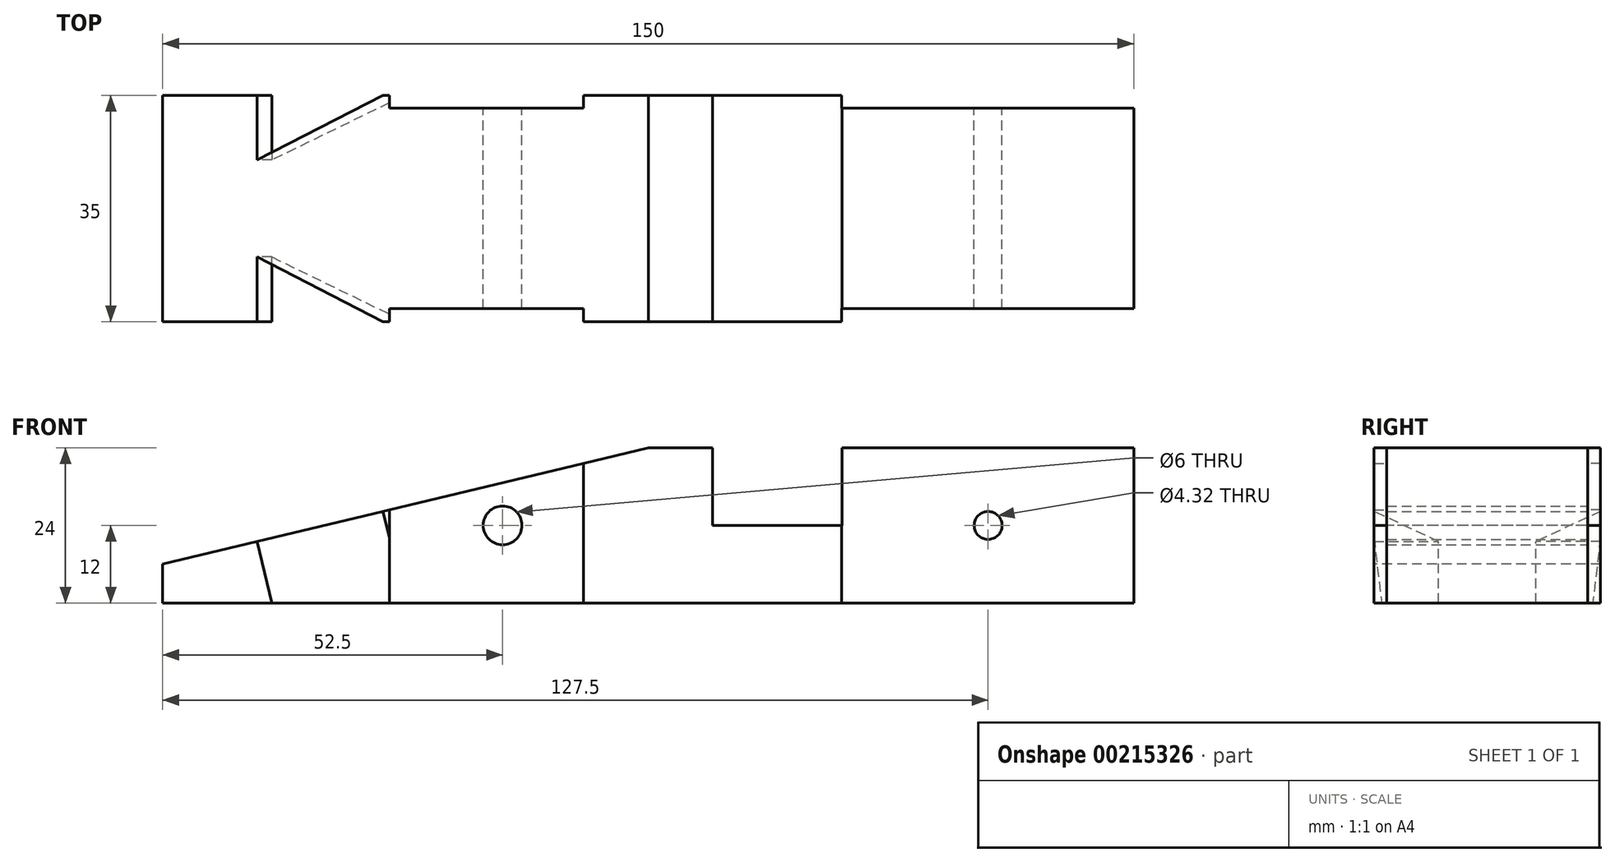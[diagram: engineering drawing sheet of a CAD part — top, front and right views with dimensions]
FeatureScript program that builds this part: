
annotation { "Feature Type Name" : "Feature", "Feature Type Description" : "" }
export const myFeature = defineFeature(function(context is Context, id is Id, definition is map)
    precondition{}
    {
        {
            var Q0;
            Q0=qCreatedBy(makeId("Front.planeOp"),FACE);
            var sketch = newSketch(context, id + "F0", { "sketchPlane" : qUnion([Q0])});
            skLineSegment(sketch, "E0.bottom", {"start": v(-75, 12) * mm, "end": v(75, 12) * mm});
            skLineSegment(sketch, "E0.top", {"start": v(-75, -12) * mm, "end": v(75, -12) * mm});
            skLineSegment(sketch, "E0.left", {"start": v(-75, 12) * mm, "end": v(-75, -12) * mm});
            skLineSegment(sketch, "E0.right", {"start": v(75, 12) * mm, "end": v(75, -12) * mm});
            skPoint(sketch, "E0.middle", {"position": v(0, 0) * mm});
            skCircle(sketch, "E1", {"center": v(-22.5, 0) * mm, "radius": 3 * mm});
            skCircle(sketch, "E2", {"center": v(52.5, 0) * mm, "radius": 2.16 * mm});
            skPoint(sketch, "E3.orphan", {"position": v(50, 12) * mm});
            skPoint(sketch, "E4.orphan", {"position": v(50, 6.5) * mm});
            skSolve(sketch);
        }
        {
            var Q0;
            Q0 = qSketchRegion(id + "F0", true);
            extrude(context, id + "F1", {"entities" : qUnion([Q0]), "depth" : 35 * mm});
        }
        {
            var Q0;
            Q0=makeQuery(id+"F1.opExtrude","CAP_FACE",FACE,{"disambiguationData":[OSD([sQuery(id+"F0.wireOp",EDGE,"E0.bottom"),sQuery(id+"F0.wireOp",EDGE,"E0.top"),sQuery(id+"F0.wireOp",EDGE,"E0.left"),sQuery(id+"F0.wireOp",EDGE,"E0.right"),sQuery(id+"F0.wireOp",EDGE,"E1"),sQuery(id+"F0.wireOp",EDGE,"E2")])],"isStart":false});
            var sketch = newSketch(context, id + "F2", { "sketchPlane" : qUnion([Q0])});
            skLineSegment(sketch, "E5", {"start": v(-75, -6) * mm, "end": v(0, 12) * mm});
            skPoint(sketch, "E6.end.orphan", {"position": v(0, -6) * mm});
            skLineSegment(sketch, "E7", {"start": v(-75, 12) * mm, "end": v(-75, -6) * mm});
            skLineSegment(sketch, "E8", {"start": v(-75, 12) * mm, "end": v(0, 12) * mm});
            skSolve(sketch);
        }
        {
            var Q0;
            Q0 = qSketchRegion(id + "F2", true);
            extrude(context, id + "F3", {"entities" : qUnion([Q0]), "operationType" : NewBodyOperationType.REMOVE, "oppositeDirection" : true, "depth" : 35 * mm});
        }
        {
            var Q0;
            Q0=makeQuery(id+"F3.boolean.opBoolean","COPY",FACE,{"derivedFrom":makeQuery(id+"F3.opExtrude","SWEPT_FACE",FACE,{"disambiguationData":[OSD([sQuery(id+"F2.wireOp",EDGE,"E5")])]})});
            var sketch = newSketch(context, id + "F4", { "sketchPlane" : qUnion([Q0])});
            skLineSegment(sketch, "E9", {"start": v(-74.33, -35) * mm, "end": v(-59.33, -35) * mm});
            skLineSegment(sketch, "E10", {"start": v(-74.33, -35) * mm, "end": v(-39.33, -35) * mm});
            skLineSegment(sketch, "E11", {"start": v(-59.33, -35) * mm, "end": v(-59.33, -25) * mm});
            skLineSegment(sketch, "E12", {"start": v(-59.33, 0) * mm, "end": v(-59.33, -10) * mm});
            skLineSegment(sketch, "E13", {"start": v(-39.33, 0) * mm, "end": v(-39.33, 0) * mm});
            skLineSegment(sketch, "E14", {"start": v(-39.33, 0) * mm, "end": v(-59.33, -10) * mm});
            skLineSegment(sketch, "E15", {"start": v(-39.33, 0) * mm, "end": v(-59.33, 0) * mm});
            skLineSegment(sketch, "E16", {"start": v(-59.33, -25) * mm, "end": v(-39.33, -35) * mm});
            skLineSegment(sketch, "E17", {"start": v(-39.33, -35) * mm, "end": v(-59.33, -35) * mm});
            skSolve(sketch);
        }
        {
            var Q0;
            Q0 = qSketchRegion(id + "F4", true);
            extrude(context, id + "F5", {"entities" : qUnion([Q0]), "operationType" : NewBodyOperationType.REMOVE, "oppositeDirection" : true, "depth" : 25 * mm});
        }
        {
            var Q0;
            {var subQ0=sQuery(id+"F0.wireOp",EDGE,"E1");var subQ1=sQuery(id+"F0.wireOp",EDGE,"E0.right");var subQ2=sQuery(id+"F0.wireOp",EDGE,"E0.top");var subQ3=sQuery(id+"F0.wireOp",EDGE,"E0.bottom");var subQ4=sQuery(id+"F0.wireOp",EDGE,"E2");Q0=makeQuery(id+"F5.boolean.opBoolean","SPLIT",FACE,{"disambiguationData":[TD([makeQuery(id+"F1.opExtrude","SWEPT_FACE",FACE,{"disambiguationData":[OSD([subQ3])]})])],"derivedFrom":makeQuery(id+"F1.opExtrude","CAP_FACE",FACE,{"disambiguationData":[OSD([subQ3,subQ2,sQuery(id+"F0.wireOp",EDGE,"E0.left"),subQ1,subQ0,subQ4])],"isStart":false})});}
            var sketch = newSketch(context, id + "F6", { "sketchPlane" : qUnion([Q0])});
            skLineSegment(sketch, "E18", {"start": v(9.92, 0) * mm, "end": v(29.92, 0) * mm});
            skLineSegment(sketch, "E19", {"start": v(9.92, 0) * mm, "end": v(9.92, 12) * mm});
            skLineSegment(sketch, "E20", {"start": v(9.92, 12) * mm, "end": v(29.92, 12) * mm});
            skLineSegment(sketch, "E21", {"start": v(29.92, 12) * mm, "end": v(29.92, 0) * mm});
            skSolve(sketch);
        }
        {
            var Q0;
            Q0 = qSketchRegion(id + "F6", true);
            extrude(context, id + "F7", {"entities" : qUnion([Q0]), "operationType" : NewBodyOperationType.REMOVE, "oppositeDirection" : true, "depth" : 35 * mm});
        }
        {
            var Q0;
            Q0=makeQuery(id+"F1.opExtrude","SWEPT_FACE",FACE,{"disambiguationData":[OSD([sQuery(id+"F0.wireOp",EDGE,"E0.top")])]});
            var sketch = newSketch(context, id + "F8", { "sketchPlane" : qUnion([Q0])});
            skLineSegment(sketch, "E22", {"start": v(-40, 35) * mm, "end": v(-10, 35) * mm});
            skLineSegment(sketch, "E23", {"start": v(-10, 35) * mm, "end": v(-10, 33) * mm});
            skLineSegment(sketch, "E24", {"start": v(-40, 35) * mm, "end": v(-40, 33) * mm});
            skLineSegment(sketch, "E25", {"start": v(-40, 33) * mm, "end": v(-10, 33) * mm});
            skLineSegment(sketch, "E26", {"start": v(-40, 0) * mm, "end": v(-40, 2) * mm});
            skLineSegment(sketch, "E27", {"start": v(-10, 0) * mm, "end": v(-10, 2) * mm});
            skLineSegment(sketch, "E28", {"start": v(-10, 2) * mm, "end": v(-40, 2) * mm});
            skLineSegment(sketch, "E29", {"start": v(-40, 0) * mm, "end": v(-10, 0) * mm});
            skSolve(sketch);
        }
        {
            var Q0;
            Q0 = qSketchRegion(id + "F8", true);
            extrude(context, id + "F9", {"entities" : qUnion([Q0]), "operationType" : NewBodyOperationType.REMOVE, "oppositeDirection" : true, "depth" : 25 * mm});
        }
        {
            var Q0;
            Q0=makeQuery(id+"F1.opExtrude","SWEPT_FACE",FACE,{"disambiguationData":[OSD([sQuery(id+"F0.wireOp",EDGE,"E0.top")])]});
            var sketch = newSketch(context, id + "F10", { "sketchPlane" : qUnion([Q0])});
            skLineSegment(sketch, "E30", {"start": v(29.9, 35) * mm, "end": v(29.9, 33) * mm});
            skLineSegment(sketch, "E31", {"start": v(29.9, 0) * mm, "end": v(29.9, 2) * mm});
            skLineSegment(sketch, "E32", {"start": v(29.9, 2) * mm, "end": v(75, 2) * mm});
            skLineSegment(sketch, "E33", {"start": v(75, 2) * mm, "end": v(75, 0) * mm});
            skLineSegment(sketch, "E34", {"start": v(75, 0) * mm, "end": v(29.9, 0) * mm});
            skLineSegment(sketch, "E35", {"start": v(29.9, 33) * mm, "end": v(75, 33) * mm});
            skLineSegment(sketch, "E36", {"start": v(75, 33) * mm, "end": v(75, 35) * mm});
            skLineSegment(sketch, "E37", {"start": v(75, 35) * mm, "end": v(29.9, 35) * mm});
            skSolve(sketch);
        }
        {
            var Q0;
            Q0 = qSketchRegion(id + "F10", true);
            extrude(context, id + "F11", {"entities" : qUnion([Q0]), "operationType" : NewBodyOperationType.REMOVE, "oppositeDirection" : true, "depth" : 25 * mm});
        }
    });
